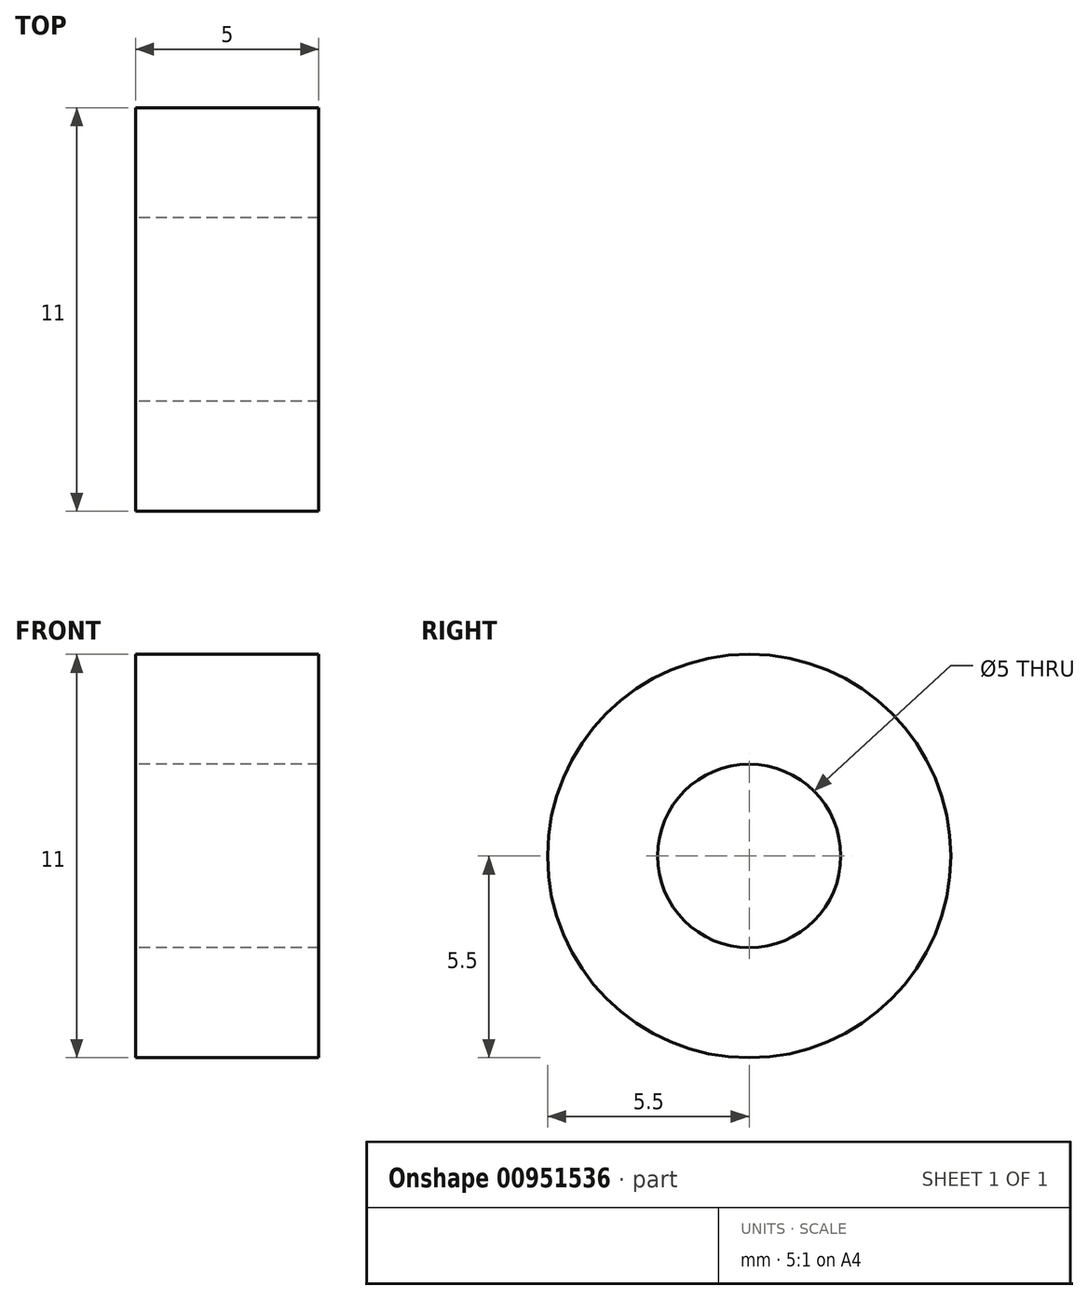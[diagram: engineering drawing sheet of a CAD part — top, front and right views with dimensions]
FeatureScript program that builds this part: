
annotation { "Feature Type Name" : "Feature", "Feature Type Description" : "" }
export const myFeature = defineFeature(function(context is Context, id is Id, definition is map)
    precondition{}
    {
        {
            var Q0;
            Q0=qCreatedBy(makeId("Right.planeOp"),FACE);
            var sketch = newSketch(context, id + "F0", { "sketchPlane" : qUnion([Q0])});
            skCircle(sketch, "E0", {"center": v(0, 0) * mm, "radius": 5.5 * mm});
            skCircle(sketch, "E1", {"center": v(0, 0) * mm, "radius": 2.5 * mm});
            skSolve(sketch);
        }
        {
            var Q0;
            Q0 = qSketchRegion(id + "F0", true);
            extrude(context, id + "F1", {"entities" : qUnion([Q0]), "depth" : 5 * mm, "offsetDistance" : 25 * mm});
        }
    });
